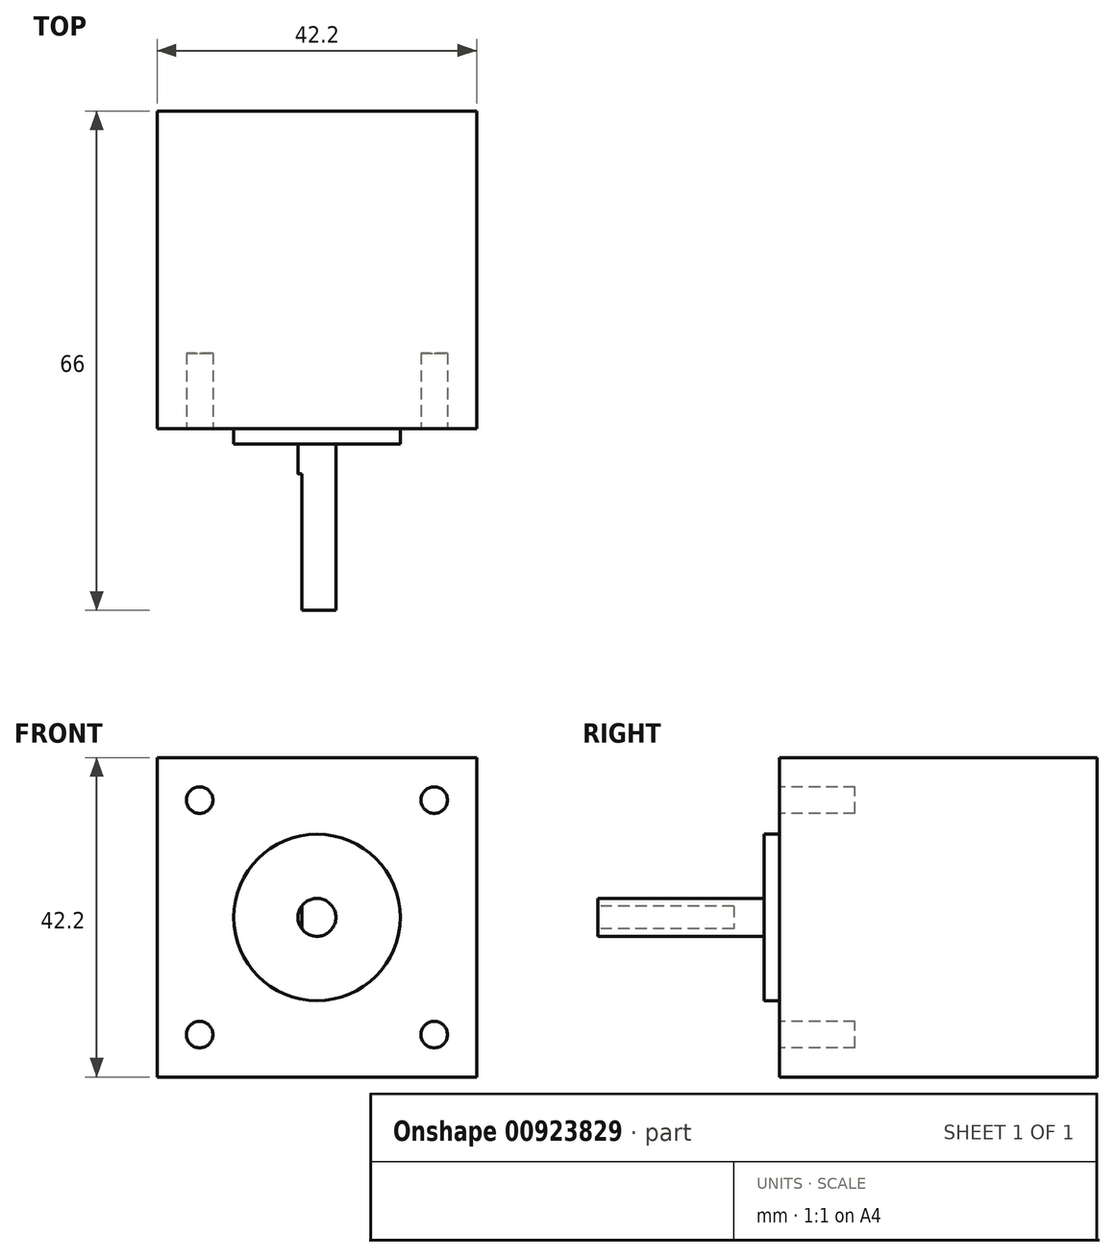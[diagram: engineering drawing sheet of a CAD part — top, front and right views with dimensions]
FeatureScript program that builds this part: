
annotation { "Feature Type Name" : "Feature", "Feature Type Description" : "" }
export const myFeature = defineFeature(function(context is Context, id is Id, definition is map)
    precondition{}
    {
        {
            var Q0;
            Q0=qCreatedBy(makeId("Front.planeOp"),FACE);
            var sketch = newSketch(context, id + "F0", { "sketchPlane" : qUnion([Q0])});
            skArc(sketch, "E0", {"start": v(2.5, 0) * mm, "mid": v(1.77, 1.77) * mm, "end": v(0, 2.5) * mm});
            skArc(sketch, "E1", {"start": v(11, 0) * mm, "mid": v(7.78, 7.78) * mm, "end": v(0, 11) * mm});
            skPoint(sketch, "E2", {"position": v(21.1, 0) * mm});
            skPoint(sketch, "E3", {"position": v(0, 21.1) * mm});
            skLineSegment(sketch, "E4", {"start": v(0, 21.1) * mm, "end": v(21.1, 21.1) * mm});
            skLineSegment(sketch, "E5", {"start": v(21.1, 21.1) * mm, "end": v(21.1, 0) * mm});
            skPoint(sketch, "E6", {"position": v(15.5, 15.5) * mm});
            skCircle(sketch, "E7", {"center": v(15.5, 15.5) * mm, "radius": 1.75 * mm});
            skLineSegment(sketch, "E8.1.0", {"start": v(-21.1, 21.1) * mm, "end": v(0, 21.1) * mm});
            skCircle(sketch, "E8.1.1", {"center": v(-15.5, 15.5) * mm, "radius": 1.75 * mm});
            skArc(sketch, "E8.1.2", {"start": v(0, 2.5) * mm, "mid": v(-1.77, 1.77) * mm, "end": v(-2.5, 0) * mm});
            skPoint(sketch, "E8.1.4", {"position": v(-15.5, 15.5) * mm});
            skArc(sketch, "E8.1.5", {"start": v(0, 11) * mm, "mid": v(-7.78, 7.78) * mm, "end": v(-11, 0) * mm});
            skLineSegment(sketch, "E8.1.7", {"start": v(-21.1, 0) * mm, "end": v(-21.1, 21.1) * mm});
            skPoint(sketch, "E8.1.8", {"position": v(-21.1, 0) * mm});
            skLineSegment(sketch, "E8.2.0", {"start": v(-21.1, -21.1) * mm, "end": v(-21.1, 0) * mm});
            skCircle(sketch, "E8.2.1", {"center": v(-15.5, -15.5) * mm, "radius": 1.75 * mm});
            skArc(sketch, "E8.2.2", {"start": v(-2.5, 0) * mm, "mid": v(-1.77, -1.77) * mm, "end": v(0, -2.5) * mm});
            skPoint(sketch, "E8.2.3", {"position": v(-21.1, 0) * mm});
            skPoint(sketch, "E8.2.4", {"position": v(-15.5, -15.5) * mm});
            skArc(sketch, "E8.2.5", {"start": v(-11, 0) * mm, "mid": v(-7.78, -7.78) * mm, "end": v(0, -11) * mm});
            skLineSegment(sketch, "E8.2.7", {"start": v(0, -21.1) * mm, "end": v(-21.1, -21.1) * mm});
            skPoint(sketch, "E8.2.8", {"position": v(0, -21.1) * mm});
            skLineSegment(sketch, "E8.3.0", {"start": v(21.1, -21.1) * mm, "end": v(0, -21.1) * mm});
            skCircle(sketch, "E8.3.1", {"center": v(15.5, -15.5) * mm, "radius": 1.75 * mm});
            skArc(sketch, "E8.3.2", {"start": v(0, -2.5) * mm, "mid": v(1.77, -1.77) * mm, "end": v(2.5, 0) * mm});
            skPoint(sketch, "E8.3.3", {"position": v(0, -21.1) * mm});
            skPoint(sketch, "E8.3.4", {"position": v(15.5, -15.5) * mm});
            skArc(sketch, "E8.3.5", {"start": v(0, -11) * mm, "mid": v(7.78, -7.78) * mm, "end": v(11, 0) * mm});
            skLineSegment(sketch, "E8.3.7", {"start": v(21.1, 0) * mm, "end": v(21.1, -21.1) * mm});
            skSolve(sketch);
        }
        {
            var Q0;
            Q0=makeQuery(id+"F0.imprint","IMPRINT",FACE,{"disambiguationData":[TD([[makeQuery(id+"F0.imprint","IMPRINT",EDGE,{"derivedFrom":sQuery(id+"F0.wireOp",EDGE,"E1")}),-1.0]])]});
            var Q1;
            Q1=makeQuery(id+"F0.imprint","IMPRINT",FACE,{"disambiguationData":[TD([[makeQuery(id+"F0.imprint","IMPRINT",EDGE,{"derivedFrom":sQuery(id+"F0.wireOp",EDGE,"E0")}),-1.0]])]});
            var Q2;
            Q2=makeQuery(id+"F0.imprint","IMPRINT",FACE,{"disambiguationData":[TD([[makeQuery(id+"F0.imprint","IMPRINT",EDGE,{"derivedFrom":sQuery(id+"F0.wireOp",EDGE,"E0")}),1.0]])]});
            var Q3;
            Q3=makeQuery(id+"F0.imprint","IMPRINT",FACE,{"disambiguationData":[TD([[makeQuery(id+"F0.imprint","IMPRINT",EDGE,{"derivedFrom":sQuery(id+"F0.wireOp",EDGE,"E7")}),1.0]])]});
            var Q4;
            Q4=makeQuery(id+"F0.imprint","IMPRINT",FACE,{"disambiguationData":[TD([[makeQuery(id+"F0.imprint","IMPRINT",EDGE,{"derivedFrom":sQuery(id+"F0.wireOp",EDGE,"E8.1.1")}),1.0]])]});
            var Q5;
            Q5=makeQuery(id+"F0.imprint","IMPRINT",FACE,{"disambiguationData":[TD([[makeQuery(id+"F0.imprint","IMPRINT",EDGE,{"derivedFrom":sQuery(id+"F0.wireOp",EDGE,"E8.2.1")}),1.0]])]});
            var Q6;
            Q6=makeQuery(id+"F0.imprint","IMPRINT",FACE,{"disambiguationData":[TD([[makeQuery(id+"F0.imprint","IMPRINT",EDGE,{"derivedFrom":sQuery(id+"F0.wireOp",EDGE,"E8.3.1")}),1.0]])]});
            extrude(context, id + "F1", {"entities" : qUnion([Q0, Q1, Q2, Q3, Q4, Q5, Q6]), "oppositeDirection" : true, "depth" : 42 * mm, "offsetDistance" : 25 * mm});
        }
        {
            var Q0;
            Q0=makeQuery(id+"F0.imprint","IMPRINT",FACE,{"disambiguationData":[TD([[makeQuery(id+"F0.imprint","IMPRINT",EDGE,{"derivedFrom":sQuery(id+"F0.wireOp",EDGE,"E0")}),-1.0]])]});
            extrude(context, id + "F2", {"entities" : qUnion([Q0]), "operationType" : NewBodyOperationType.ADD, "depth" : 2 * mm, "offsetDistance" : 25 * mm});
        }
        {
            var Q0;
            Q0=makeQuery(id+"F0.imprint","IMPRINT",FACE,{"disambiguationData":[TD([[makeQuery(id+"F0.imprint","IMPRINT",EDGE,{"derivedFrom":sQuery(id+"F0.wireOp",EDGE,"E0")}),1.0]])]});
            extrude(context, id + "F3", {"entities" : qUnion([Q0]), "operationType" : NewBodyOperationType.ADD, "depth" : 24 * mm, "offsetDistance" : 25 * mm});
        }
        {
            var Q0;
            Q0=makeQuery(id+"F0.imprint","IMPRINT",FACE,{"disambiguationData":[TD([[makeQuery(id+"F0.imprint","IMPRINT",EDGE,{"derivedFrom":sQuery(id+"F0.wireOp",EDGE,"E8.1.1")}),1.0]])]});
            var Q1;
            Q1=makeQuery(id+"F0.imprint","IMPRINT",FACE,{"disambiguationData":[TD([[makeQuery(id+"F0.imprint","IMPRINT",EDGE,{"derivedFrom":sQuery(id+"F0.wireOp",EDGE,"E8.3.1")}),1.0]])]});
            var Q2;
            Q2=makeQuery(id+"F0.imprint","IMPRINT",FACE,{"disambiguationData":[TD([[makeQuery(id+"F0.imprint","IMPRINT",EDGE,{"derivedFrom":sQuery(id+"F0.wireOp",EDGE,"E8.2.1")}),1.0]])]});
            var Q3;
            Q3=makeQuery(id+"F0.imprint","IMPRINT",FACE,{"disambiguationData":[TD([[makeQuery(id+"F0.imprint","IMPRINT",EDGE,{"derivedFrom":sQuery(id+"F0.wireOp",EDGE,"E7")}),1.0]])]});
            extrude(context, id + "F4", {"entities" : qUnion([Q0, Q1, Q2, Q3]), "operationType" : NewBodyOperationType.REMOVE, "oppositeDirection" : true, "depth" : 10 * mm, "offsetDistance" : 25 * mm});
        }
        {
            var Q0;
            Q0=makeQuery(id+"F3.opExtrude","CAP_FACE",FACE,{"disambiguationData":[OSD([sQuery(id+"F0.wireOp",EDGE,"E0"),sQuery(id+"F0.wireOp",EDGE,"E8.1.2"),sQuery(id+"F0.wireOp",EDGE,"E8.2.2"),sQuery(id+"F0.wireOp",EDGE,"E8.3.2")])],"isStart":false});
            var sketch = newSketch(context, id + "F5", { "sketchPlane" : qUnion([Q0])});
            skCircle(sketch, "E9", {"center": v(0, 0) * mm, "radius": 2.5 * mm});
            skCircle(sketch, "E10", {"center": v(0, 0) * mm, "radius": 2 * mm});
            skLineSegment(sketch, "E11", {"start": v(-2, 0) * mm, "end": v(-2, 1.5) * mm});
            skLineSegment(sketch, "E12", {"start": v(-2, 0) * mm, "end": v(-2, -1.5) * mm});
            skSolve(sketch);
        }
        {
            var Q0;
            {var subQ0=sQuery(id+"F5.wireOp",EDGE,"E11");Q0=makeQuery(id+"F5.imprint","IMPRINT",FACE,{"disambiguationData":[TD([[makeQuery(id+"F5.imprint","IMPRINT",EDGE,{"derivedFrom":subQ0}),1.0]])]});}
            extrude(context, id + "F6", {"entities" : qUnion([Q0]), "operationType" : NewBodyOperationType.REMOVE, "oppositeDirection" : true, "depth" : 18 * mm, "offsetDistance" : 25 * mm});
        }
    });
